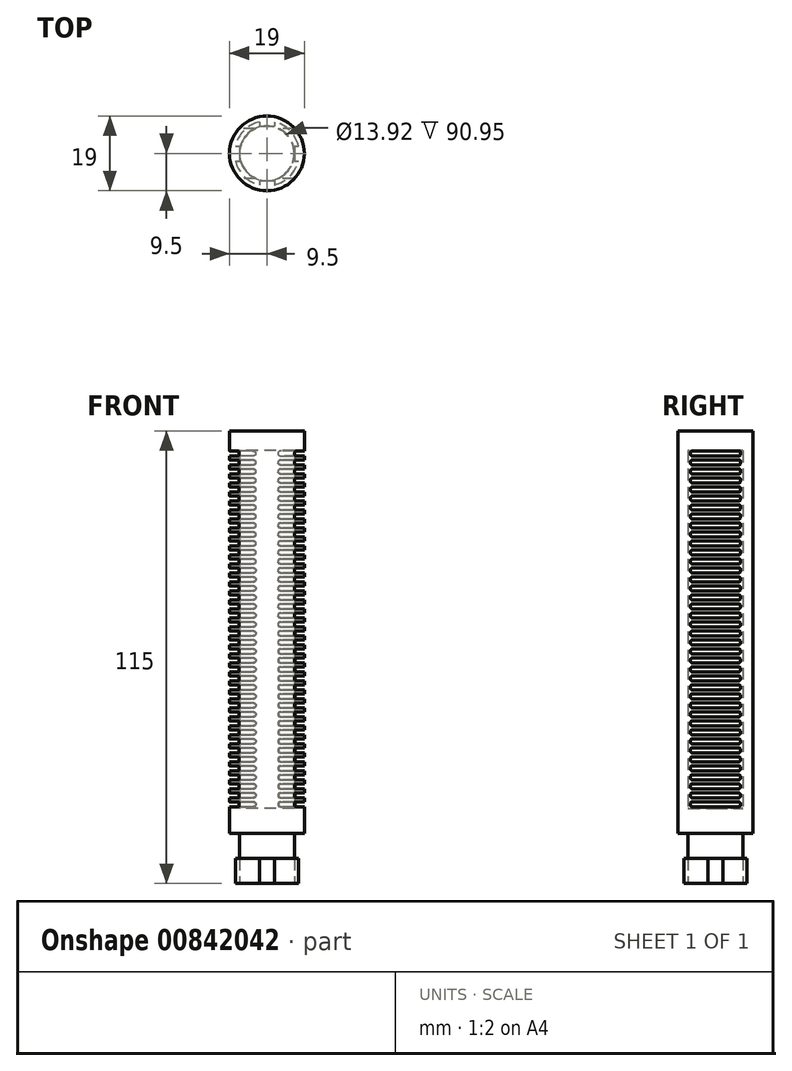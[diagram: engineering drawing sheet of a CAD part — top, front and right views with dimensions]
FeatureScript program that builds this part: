
annotation { "Feature Type Name" : "Feature", "Feature Type Description" : "" }
export const myFeature = defineFeature(function(context is Context, id is Id, definition is map)
    precondition{}
    {
        {
            var Q0;
            Q0=qCreatedBy(makeId("Top.planeOp"),FACE);
            var sketch = newSketch(context, id + "F0", { "sketchPlane" : qUnion([Q0])});
            skCircle(sketch, "E0", {"center": v(0, 0) * mm, "radius": 9.5 * mm});
            skSolve(sketch);
        }
        {
            var Q0;
            Q0 = qSketchRegion(id + "F0", true);
            extrude(context, id + "F1", {"entities" : qUnion([Q0]), "depth" : 115 * mm, "offsetDistance" : 25.4 * mm});
        }
        {
            var Q0;
            Q0=qCreatedBy(makeId("Top.planeOp"),FACE);
            var sketch = newSketch(context, id + "F2", { "sketchPlane" : qUnion([Q0])});
            skCircle(sketch, "E1", {"center": v(0, 0) * mm, "radius": 9.5 * mm});
            skCircle(sketch, "E2.0", {"center": v(0, 0) * mm, "radius": 6.96 * mm});
            skSolve(sketch);
        }
        {
            var Q0;
            Q0=makeQuery(id+"F2.imprint","IMPRINT",FACE,{"disambiguationData":[TD([[makeQuery(id+"F2.imprint","IMPRINT",EDGE,{"derivedFrom":sQuery(id+"F2.wireOp",EDGE,"E1")}),1.0]])]});
            extrude(context, id + "F3", {"entities" : qUnion([Q0]), "depth" : 12.7 * mm, "offsetDistance" : 25.4 * mm, "hasSecondDirection" : true, "secondDirectionOppositeDirection" : true, "secondDirectionDepth" : -6.35 * mm});
        }
        {
            var Q0;
            Q0=makeQuery(id+"F3.opExtrude","SWEPT_BODY",BODY,{"disambiguationData":[OSD([sQuery(id+"F2.wireOp",EDGE,"E1"),sQuery(id+"F2.wireOp",EDGE,"E2.0")])]});
            var Q1;
            Q1=makeQuery(id+"F1.opExtrude","SWEPT_BODY",BODY,{"disambiguationData":[OSD([sQuery(id+"F0.wireOp",EDGE,"E0")])]});
            booleanBodies(context, id + "F4", {"operationType" : BooleanOperationType.SUBTRACTION, "tools" : qUnion([Q0]), "targets" : qUnion([Q1])});
        }
        {
            var Q0;
            Q0=qCreatedBy(makeId("Top.planeOp"),FACE);
            var sketch = newSketch(context, id + "F5", { "sketchPlane" : qUnion([Q0])});
            skCircle(sketch, "E3", {"center": v(0, 0) * mm, "radius": 9.5 * mm});
            skCircle(sketch, "E4.0", {"center": v(0, 0) * mm, "radius": 8.23 * mm});
            skSolve(sketch);
        }
        {
            var Q0;
            Q0=makeQuery(id+"F5.imprint","IMPRINT",FACE,{"disambiguationData":[TD([[makeQuery(id+"F5.imprint","IMPRINT",EDGE,{"derivedFrom":sQuery(id+"F5.wireOp",EDGE,"E3")}),1.0]])]});
            extrude(context, id + "F6", {"entities" : qUnion([Q0]), "depth" : 6.35 * mm, "offsetDistance" : 25.4 * mm});
        }
        {
            var Q0;
            Q0=makeQuery(id+"F6.opExtrude","SWEPT_BODY",BODY,{"disambiguationData":[OSD([sQuery(id+"F5.wireOp",EDGE,"E3"),sQuery(id+"F5.wireOp",EDGE,"E4.0")])]});
            var Q1;
            Q1=makeQuery(id+"F1.opExtrude","SWEPT_BODY",BODY,{"disambiguationData":[OSD([sQuery(id+"F0.wireOp",EDGE,"E0")])]});
            booleanBodies(context, id + "F7", {"operationType" : BooleanOperationType.SUBTRACTION, "tools" : qUnion([Q0]), "targets" : qUnion([Q1])});
        }
        {
            var Q0;
            Q0=qCreatedBy(makeId("Top.planeOp"),FACE);
            var sketch = newSketch(context, id + "F8", { "sketchPlane" : qUnion([Q0])});
            skCircle(sketch, "E5", {"center": v(0, 0) * mm, "radius": 9.5 * mm, "construction": true});
            skCircle(sketch, "E6.0", {"center": v(0, 0) * mm, "radius": 6.96 * mm, "construction": true});
            skLineSegment(sketch, "E7.bottom", {"start": v(-1.9, 10.77) * mm, "end": v(1.9, 10.77) * mm});
            skLineSegment(sketch, "E7.top", {"start": v(-1.9, 6.96) * mm, "end": v(1.9, 6.96) * mm});
            skLineSegment(sketch, "E7.left", {"start": v(-1.9, 10.77) * mm, "end": v(-1.9, 6.96) * mm});
            skLineSegment(sketch, "E7.right", {"start": v(1.9, 10.77) * mm, "end": v(1.9, 6.96) * mm});
            skPoint(sketch, "E8", {"position": v(0, 6.96) * mm});
            skLineSegment(sketch, "E9.bottom", {"start": v(-9.5, 9.5) * mm, "end": v(9.5, 9.5) * mm, "construction": true});
            skLineSegment(sketch, "E9.top", {"start": v(-9.5, -9.5) * mm, "end": v(9.5, -9.5) * mm, "construction": true});
            skLineSegment(sketch, "E9.left", {"start": v(-9.5, 9.5) * mm, "end": v(-9.5, -9.5) * mm, "construction": true});
            skLineSegment(sketch, "E9.right", {"start": v(9.5, 9.5) * mm, "end": v(9.5, -9.5) * mm, "construction": true});
            skPoint(sketch, "E10", {"position": v(0, -9.5) * mm});
            skPoint(sketch, "E11", {"position": v(9.5, 0) * mm});
            skLineSegment(sketch, "E12.0", {"start": v(-6.96, 6.96) * mm, "end": v(-6.96, -6.96) * mm, "construction": true});
            skLineSegment(sketch, "E12.1", {"start": v(-6.96, 6.96) * mm, "end": v(6.96, 6.96) * mm, "construction": true});
            skLineSegment(sketch, "E12.2", {"start": v(6.96, 6.96) * mm, "end": v(6.96, -6.96) * mm, "construction": true});
            skLineSegment(sketch, "E12.3", {"start": v(-6.96, -6.96) * mm, "end": v(6.96, -6.96) * mm, "construction": true});
            skLineSegment(sketch, "E13.bottom", {"start": v(6.96, 1.9) * mm, "end": v(10.77, 1.9) * mm});
            skLineSegment(sketch, "E13.top", {"start": v(6.96, -1.9) * mm, "end": v(10.77, -1.9) * mm});
            skLineSegment(sketch, "E13.left", {"start": v(6.96, 1.9) * mm, "end": v(6.96, -1.9) * mm});
            skLineSegment(sketch, "E13.right", {"start": v(10.77, 1.9) * mm, "end": v(10.77, -1.9) * mm});
            skPoint(sketch, "E14", {"position": v(6.96, 0) * mm});
            skLineSegment(sketch, "E15.bottom", {"start": v(-1.9, -6.96) * mm, "end": v(1.9, -6.96) * mm});
            skLineSegment(sketch, "E15.top", {"start": v(-1.9, -10.77) * mm, "end": v(1.9, -10.77) * mm});
            skLineSegment(sketch, "E15.left", {"start": v(-1.9, -6.96) * mm, "end": v(-1.9, -10.77) * mm});
            skLineSegment(sketch, "E15.right", {"start": v(1.9, -6.96) * mm, "end": v(1.9, -10.77) * mm});
            skPoint(sketch, "E16", {"position": v(0, -6.96) * mm});
            skLineSegment(sketch, "E17.bottom", {"start": v(-10.77, 1.9) * mm, "end": v(-6.96, 1.9) * mm});
            skLineSegment(sketch, "E17.top", {"start": v(-10.77, -1.9) * mm, "end": v(-6.96, -1.9) * mm});
            skLineSegment(sketch, "E17.left", {"start": v(-10.77, 1.9) * mm, "end": v(-10.77, -1.9) * mm});
            skLineSegment(sketch, "E17.right", {"start": v(-6.96, 1.9) * mm, "end": v(-6.96, -1.9) * mm});
            skPoint(sketch, "E18", {"position": v(-6.96, 0) * mm});
            skSolve(sketch);
        }
        {
            var Q0;
            Q0=makeQuery(id+"F8.imprint","IMPRINT",FACE,{"disambiguationData":[TD([[makeQuery(id+"F8.imprint","IMPRINT",EDGE,{"derivedFrom":sQuery(id+"F8.wireOp",EDGE,"E17.bottom")}),-1.0]])]});
            var Q1;
            Q1=makeQuery(id+"F8.imprint","IMPRINT",FACE,{"disambiguationData":[TD([[makeQuery(id+"F8.imprint","IMPRINT",EDGE,{"derivedFrom":sQuery(id+"F8.wireOp",EDGE,"E7.bottom")}),-1.0]])]});
            var Q2;
            Q2=makeQuery(id+"F8.imprint","IMPRINT",FACE,{"disambiguationData":[TD([[makeQuery(id+"F8.imprint","IMPRINT",EDGE,{"derivedFrom":sQuery(id+"F8.wireOp",EDGE,"E13.bottom")}),-1.0]])]});
            var Q3;
            Q3=makeQuery(id+"F8.imprint","IMPRINT",FACE,{"disambiguationData":[TD([[makeQuery(id+"F8.imprint","IMPRINT",EDGE,{"derivedFrom":sQuery(id+"F8.wireOp",EDGE,"E15.bottom")}),-1.0]])]});
            extrude(context, id + "F9", {"entities" : qUnion([Q0, Q1, Q2, Q3]), "depth" : 6.35 * mm, "offsetDistance" : 25.4 * mm});
        }
        {
            var Q0;
            Q0=makeQuery(id+"F9.opExtrude","SWEPT_BODY",BODY,{"disambiguationData":[OSD([sQuery(id+"F8.wireOp",EDGE,"E7.bottom"),sQuery(id+"F8.wireOp",EDGE,"E7.top"),sQuery(id+"F8.wireOp",EDGE,"E7.left"),sQuery(id+"F8.wireOp",EDGE,"E7.right")])]});
            var Q1;
            Q1=makeQuery(id+"F9.opExtrude","SWEPT_BODY",BODY,{"disambiguationData":[OSD([sQuery(id+"F8.wireOp",EDGE,"E13.bottom"),sQuery(id+"F8.wireOp",EDGE,"E13.top"),sQuery(id+"F8.wireOp",EDGE,"E13.left"),sQuery(id+"F8.wireOp",EDGE,"E13.right")])]});
            var Q2;
            Q2=makeQuery(id+"F9.opExtrude","SWEPT_BODY",BODY,{"disambiguationData":[OSD([sQuery(id+"F8.wireOp",EDGE,"E15.bottom"),sQuery(id+"F8.wireOp",EDGE,"E15.top"),sQuery(id+"F8.wireOp",EDGE,"E15.left"),sQuery(id+"F8.wireOp",EDGE,"E15.right")])]});
            var Q3;
            Q3=makeQuery(id+"F9.opExtrude","SWEPT_BODY",BODY,{"disambiguationData":[OSD([sQuery(id+"F8.wireOp",EDGE,"E17.bottom"),sQuery(id+"F8.wireOp",EDGE,"E17.top"),sQuery(id+"F8.wireOp",EDGE,"E17.left"),sQuery(id+"F8.wireOp",EDGE,"E17.right")])]});
            var Q4;
            Q4=makeQuery(id+"F1.opExtrude","SWEPT_BODY",BODY,{"disambiguationData":[OSD([sQuery(id+"F0.wireOp",EDGE,"E0")])]});
            booleanBodies(context, id + "F10", {"operationType" : BooleanOperationType.SUBTRACTION, "tools" : qUnion([Q0, Q1, Q2, Q3]), "targets" : qUnion([Q4])});
        }
        {
            var Q0;
            Q0=qCreatedBy(makeId("Top.planeOp"),FACE);
            var sketch = newSketch(context, id + "F11", { "sketchPlane" : qUnion([Q0])});
            skCircle(sketch, "E19", {"center": v(0, 0) * mm, "radius": 9.5 * mm, "construction": true});
            skCircle(sketch, "E20.0", {"center": v(0, 0) * mm, "radius": 6.96 * mm});
            skSolve(sketch);
        }
        {
            var Q0;
            Q0=makeQuery(id+"F11.imprint","IMPRINT",FACE,{"disambiguationData":[TD([[makeQuery(id+"F11.imprint","IMPRINT",EDGE,{"derivedFrom":sQuery(id+"F11.wireOp",EDGE,"E20.0")}),1.0]])]});
            extrude(context, id + "F12", {"entities" : qUnion([Q0]), "operationType" : NewBodyOperationType.REMOVE, "depth" : 110 * mm, "offsetDistance" : 25.4 * mm, "hasSecondDirection" : true, "secondDirectionOppositeDirection" : true, "secondDirectionDepth" : -19.05 * mm});
        }
        {
            var Q0;
            Q0=qCreatedBy(makeId("Right.planeOp"),FACE);
            var sketch = newSketch(context, id + "F13", { "sketchPlane" : qUnion([Q0])});
            skLineSegment(sketch, "E21.bottom", {"start": v(5.91, 109.9) * mm, "end": v(-5.91, 109.9) * mm});
            skLineSegment(sketch, "E21.top", {"start": v(5.91, 108.63) * mm, "end": v(-5.91, 108.63) * mm});
            skLineSegment(sketch, "E21.left", {"start": v(6.35, 109.46) * mm, "end": v(6.35, 109.06) * mm});
            skLineSegment(sketch, "E21.right", {"start": v(-6.35, 109.46) * mm, "end": v(-6.35, 109.06) * mm});
            skPoint(sketch, "E22", {"position": v(0, 109.9) * mm});
            skPoint(sketch, "E23.visualSharp", {"position": v(6.35, 109.9) * mm});
            skArc(sketch, "E23.filletArc", {"start": v(6.35, 109.46) * mm, "mid": v(6.22, 109.77) * mm, "end": v(5.91, 109.9) * mm});
            skPoint(sketch, "E24.visualSharp", {"position": v(6.35, 108.63) * mm});
            skArc(sketch, "E24.filletArc", {"start": v(5.91, 108.63) * mm, "mid": v(6.22, 108.75) * mm, "end": v(6.35, 109.06) * mm});
            skPoint(sketch, "E25.visualSharp", {"position": v(-6.35, 108.63) * mm});
            skArc(sketch, "E25.filletArc", {"start": v(-6.35, 109.06) * mm, "mid": v(-6.22, 108.75) * mm, "end": v(-5.91, 108.63) * mm});
            skPoint(sketch, "E26.visualSharp", {"position": v(-6.35, 109.9) * mm});
            skArc(sketch, "E26.filletArc", {"start": v(-5.91, 109.9) * mm, "mid": v(-6.22, 109.77) * mm, "end": v(-6.35, 109.46) * mm});
            skArc(sketch, "E27.1.0.0", {"start": v(6.35, 107.17) * mm, "mid": v(6.22, 107.48) * mm, "end": v(5.9, 107.6) * mm});
            skLineSegment(sketch, "E27.1.0.1", {"start": v(5.9, 107.6) * mm, "end": v(-5.91, 107.6) * mm});
            skArc(sketch, "E27.1.0.2", {"start": v(-5.91, 107.6) * mm, "mid": v(-6.22, 107.48) * mm, "end": v(-6.35, 107.17) * mm});
            skLineSegment(sketch, "E27.1.0.3", {"start": v(-6.35, 107.17) * mm, "end": v(-6.35, 106.78) * mm});
            skArc(sketch, "E27.1.0.4", {"start": v(-6.35, 106.78) * mm, "mid": v(-6.22, 106.47) * mm, "end": v(-5.91, 106.34) * mm});
            skLineSegment(sketch, "E27.1.0.5", {"start": v(5.9, 106.34) * mm, "end": v(-5.91, 106.34) * mm});
            skArc(sketch, "E27.1.0.6", {"start": v(5.9, 106.34) * mm, "mid": v(6.22, 106.47) * mm, "end": v(6.35, 106.78) * mm});
            skLineSegment(sketch, "E27.1.0.7", {"start": v(6.35, 107.17) * mm, "end": v(6.35, 106.78) * mm});
            skArc(sketch, "E27.2.0.0", {"start": v(6.35, 104.88) * mm, "mid": v(6.22, 105.2) * mm, "end": v(5.9, 105.32) * mm});
            skLineSegment(sketch, "E27.2.0.1", {"start": v(5.9, 105.32) * mm, "end": v(-5.91, 105.32) * mm});
            skArc(sketch, "E27.2.0.2", {"start": v(-5.91, 105.32) * mm, "mid": v(-6.22, 105.2) * mm, "end": v(-6.35, 104.88) * mm});
            skLineSegment(sketch, "E27.2.0.3", {"start": v(-6.35, 104.88) * mm, "end": v(-6.35, 104.5) * mm});
            skArc(sketch, "E27.2.0.4", {"start": v(-6.35, 104.5) * mm, "mid": v(-6.22, 104.18) * mm, "end": v(-5.91, 104.05) * mm});
            skLineSegment(sketch, "E27.2.0.5", {"start": v(5.9, 104.05) * mm, "end": v(-5.91, 104.05) * mm});
            skArc(sketch, "E27.2.0.6", {"start": v(5.9, 104.05) * mm, "mid": v(6.22, 104.18) * mm, "end": v(6.35, 104.5) * mm});
            skLineSegment(sketch, "E27.2.0.7", {"start": v(6.35, 104.88) * mm, "end": v(6.35, 104.5) * mm});
            skArc(sketch, "E27.3.0.0", {"start": v(6.35, 102.6) * mm, "mid": v(6.22, 102.9) * mm, "end": v(5.9, 103.04) * mm});
            skLineSegment(sketch, "E27.3.0.1", {"start": v(5.9, 103.04) * mm, "end": v(-5.91, 103.04) * mm});
            skArc(sketch, "E27.3.0.2", {"start": v(-5.91, 103.04) * mm, "mid": v(-6.22, 102.9) * mm, "end": v(-6.35, 102.6) * mm});
            skLineSegment(sketch, "E27.3.0.3", {"start": v(-6.35, 102.6) * mm, "end": v(-6.35, 102.2) * mm});
            skArc(sketch, "E27.3.0.4", {"start": v(-6.35, 102.2) * mm, "mid": v(-6.22, 101.9) * mm, "end": v(-5.91, 101.77) * mm});
            skLineSegment(sketch, "E27.3.0.5", {"start": v(5.9, 101.77) * mm, "end": v(-5.91, 101.77) * mm});
            skArc(sketch, "E27.3.0.6", {"start": v(5.9, 101.77) * mm, "mid": v(6.22, 101.9) * mm, "end": v(6.35, 102.2) * mm});
            skLineSegment(sketch, "E27.3.0.7", {"start": v(6.35, 102.6) * mm, "end": v(6.35, 102.2) * mm});
            skArc(sketch, "E27.4.0.0", {"start": v(6.35, 100.31) * mm, "mid": v(6.22, 100.62) * mm, "end": v(5.9, 100.75) * mm});
            skLineSegment(sketch, "E27.4.0.1", {"start": v(5.9, 100.75) * mm, "end": v(-5.91, 100.75) * mm});
            skArc(sketch, "E27.4.0.2", {"start": v(-5.91, 100.75) * mm, "mid": v(-6.22, 100.62) * mm, "end": v(-6.35, 100.31) * mm});
            skLineSegment(sketch, "E27.4.0.3", {"start": v(-6.35, 100.31) * mm, "end": v(-6.35, 99.92) * mm});
            skArc(sketch, "E27.4.0.4", {"start": v(-6.35, 99.92) * mm, "mid": v(-6.22, 99.61) * mm, "end": v(-5.91, 99.48) * mm});
            skLineSegment(sketch, "E27.4.0.5", {"start": v(5.9, 99.48) * mm, "end": v(-5.91, 99.48) * mm});
            skArc(sketch, "E27.4.0.6", {"start": v(5.9, 99.48) * mm, "mid": v(6.22, 99.61) * mm, "end": v(6.35, 99.92) * mm});
            skLineSegment(sketch, "E27.4.0.7", {"start": v(6.35, 100.31) * mm, "end": v(6.35, 99.92) * mm});
            skArc(sketch, "E27.5.0.0", {"start": v(6.35, 98.03) * mm, "mid": v(6.22, 98.34) * mm, "end": v(5.9, 98.47) * mm});
            skLineSegment(sketch, "E27.5.0.1", {"start": v(5.9, 98.47) * mm, "end": v(-5.91, 98.47) * mm});
            skArc(sketch, "E27.5.0.2", {"start": v(-5.91, 98.47) * mm, "mid": v(-6.23, 98.34) * mm, "end": v(-6.35, 98.03) * mm});
            skLineSegment(sketch, "E27.5.0.3", {"start": v(-6.35, 98.03) * mm, "end": v(-6.35, 97.63) * mm});
            skArc(sketch, "E27.5.0.4", {"start": v(-6.35, 97.63) * mm, "mid": v(-6.23, 97.32) * mm, "end": v(-5.91, 97.2) * mm});
            skLineSegment(sketch, "E27.5.0.5", {"start": v(5.9, 97.2) * mm, "end": v(-5.91, 97.2) * mm});
            skArc(sketch, "E27.5.0.6", {"start": v(5.9, 97.2) * mm, "mid": v(6.22, 97.32) * mm, "end": v(6.35, 97.63) * mm});
            skLineSegment(sketch, "E27.5.0.7", {"start": v(6.35, 98.03) * mm, "end": v(6.35, 97.63) * mm});
            skArc(sketch, "E27.6.0.0", {"start": v(6.34, 95.74) * mm, "mid": v(6.22, 96.05) * mm, "end": v(5.9, 96.18) * mm});
            skLineSegment(sketch, "E27.6.0.1", {"start": v(5.9, 96.18) * mm, "end": v(-5.92, 96.18) * mm});
            skArc(sketch, "E27.6.0.2", {"start": v(-5.92, 96.18) * mm, "mid": v(-6.23, 96.05) * mm, "end": v(-6.36, 95.74) * mm});
            skLineSegment(sketch, "E27.6.0.3", {"start": v(-6.36, 95.74) * mm, "end": v(-6.36, 95.35) * mm});
            skArc(sketch, "E27.6.0.4", {"start": v(-6.36, 95.35) * mm, "mid": v(-6.23, 95.04) * mm, "end": v(-5.92, 94.9) * mm});
            skLineSegment(sketch, "E27.6.0.5", {"start": v(5.9, 94.9) * mm, "end": v(-5.92, 94.9) * mm});
            skArc(sketch, "E27.6.0.6", {"start": v(5.9, 94.9) * mm, "mid": v(6.22, 95.04) * mm, "end": v(6.34, 95.35) * mm});
            skLineSegment(sketch, "E27.6.0.7", {"start": v(6.34, 95.74) * mm, "end": v(6.34, 95.35) * mm});
            skArc(sketch, "E27.7.0.0", {"start": v(6.34, 93.45) * mm, "mid": v(6.22, 93.77) * mm, "end": v(5.9, 93.9) * mm});
            skLineSegment(sketch, "E27.7.0.1", {"start": v(5.9, 93.9) * mm, "end": v(-5.92, 93.9) * mm});
            skArc(sketch, "E27.7.0.2", {"start": v(-5.92, 93.9) * mm, "mid": v(-6.23, 93.77) * mm, "end": v(-6.36, 93.45) * mm});
            skLineSegment(sketch, "E27.7.0.3", {"start": v(-6.36, 93.45) * mm, "end": v(-6.36, 93.06) * mm});
            skArc(sketch, "E27.7.0.4", {"start": v(-6.36, 93.06) * mm, "mid": v(-6.23, 92.75) * mm, "end": v(-5.92, 92.62) * mm});
            skLineSegment(sketch, "E27.7.0.5", {"start": v(5.9, 92.62) * mm, "end": v(-5.92, 92.62) * mm});
            skArc(sketch, "E27.7.0.6", {"start": v(5.9, 92.62) * mm, "mid": v(6.22, 92.75) * mm, "end": v(6.34, 93.06) * mm});
            skLineSegment(sketch, "E27.7.0.7", {"start": v(6.34, 93.45) * mm, "end": v(6.34, 93.06) * mm});
            skArc(sketch, "E27.8.0.0", {"start": v(6.34, 91.17) * mm, "mid": v(6.21, 91.48) * mm, "end": v(5.9, 91.6) * mm});
            skLineSegment(sketch, "E27.8.0.1", {"start": v(5.9, 91.6) * mm, "end": v(-5.92, 91.6) * mm});
            skArc(sketch, "E27.8.0.2", {"start": v(-5.92, 91.6) * mm, "mid": v(-6.23, 91.48) * mm, "end": v(-6.36, 91.17) * mm});
            skLineSegment(sketch, "E27.8.0.3", {"start": v(-6.36, 91.17) * mm, "end": v(-6.36, 90.78) * mm});
            skArc(sketch, "E27.8.0.4", {"start": v(-6.36, 90.78) * mm, "mid": v(-6.23, 90.47) * mm, "end": v(-5.92, 90.34) * mm});
            skLineSegment(sketch, "E27.8.0.5", {"start": v(5.9, 90.34) * mm, "end": v(-5.92, 90.34) * mm});
            skArc(sketch, "E27.8.0.6", {"start": v(5.9, 90.34) * mm, "mid": v(6.21, 90.47) * mm, "end": v(6.34, 90.78) * mm});
            skLineSegment(sketch, "E27.8.0.7", {"start": v(6.34, 91.17) * mm, "end": v(6.34, 90.78) * mm});
            skArc(sketch, "E27.9.0.0", {"start": v(6.34, 88.88) * mm, "mid": v(6.21, 89.2) * mm, "end": v(5.9, 89.32) * mm});
            skLineSegment(sketch, "E27.9.0.1", {"start": v(5.9, 89.32) * mm, "end": v(-5.92, 89.32) * mm});
            skArc(sketch, "E27.9.0.2", {"start": v(-5.92, 89.32) * mm, "mid": v(-6.23, 89.2) * mm, "end": v(-6.36, 88.88) * mm});
            skLineSegment(sketch, "E27.9.0.3", {"start": v(-6.36, 88.88) * mm, "end": v(-6.36, 88.5) * mm});
            skArc(sketch, "E27.9.0.4", {"start": v(-6.36, 88.5) * mm, "mid": v(-6.23, 88.18) * mm, "end": v(-5.92, 88.05) * mm});
            skLineSegment(sketch, "E27.9.0.5", {"start": v(5.9, 88.05) * mm, "end": v(-5.92, 88.05) * mm});
            skArc(sketch, "E27.9.0.6", {"start": v(5.9, 88.05) * mm, "mid": v(6.21, 88.18) * mm, "end": v(6.34, 88.5) * mm});
            skLineSegment(sketch, "E27.9.0.7", {"start": v(6.34, 88.88) * mm, "end": v(6.34, 88.5) * mm});
            skArc(sketch, "E27.10.0.0", {"start": v(6.34, 86.6) * mm, "mid": v(6.21, 86.9) * mm, "end": v(5.9, 87.04) * mm});
            skLineSegment(sketch, "E27.10.0.1", {"start": v(5.9, 87.04) * mm, "end": v(-5.92, 87.04) * mm});
            skArc(sketch, "E27.10.0.2", {"start": v(-5.92, 87.04) * mm, "mid": v(-6.23, 86.9) * mm, "end": v(-6.36, 86.6) * mm});
            skLineSegment(sketch, "E27.10.0.3", {"start": v(-6.36, 86.6) * mm, "end": v(-6.36, 86.2) * mm});
            skArc(sketch, "E27.10.0.4", {"start": v(-6.36, 86.2) * mm, "mid": v(-6.23, 85.9) * mm, "end": v(-5.92, 85.77) * mm});
            skLineSegment(sketch, "E27.10.0.5", {"start": v(5.9, 85.77) * mm, "end": v(-5.92, 85.77) * mm});
            skArc(sketch, "E27.10.0.6", {"start": v(5.9, 85.77) * mm, "mid": v(6.21, 85.9) * mm, "end": v(6.34, 86.2) * mm});
            skLineSegment(sketch, "E27.10.0.7", {"start": v(6.34, 86.6) * mm, "end": v(6.34, 86.2) * mm});
            skArc(sketch, "E27.11.0.0", {"start": v(6.34, 84.31) * mm, "mid": v(6.21, 84.62) * mm, "end": v(5.9, 84.75) * mm});
            skLineSegment(sketch, "E27.11.0.1", {"start": v(5.9, 84.75) * mm, "end": v(-5.92, 84.75) * mm});
            skArc(sketch, "E27.11.0.2", {"start": v(-5.92, 84.75) * mm, "mid": v(-6.23, 84.62) * mm, "end": v(-6.36, 84.31) * mm});
            skLineSegment(sketch, "E27.11.0.3", {"start": v(-6.36, 84.31) * mm, "end": v(-6.36, 83.92) * mm});
            skArc(sketch, "E27.11.0.4", {"start": v(-6.36, 83.92) * mm, "mid": v(-6.23, 83.6) * mm, "end": v(-5.92, 83.48) * mm});
            skLineSegment(sketch, "E27.11.0.5", {"start": v(5.9, 83.48) * mm, "end": v(-5.92, 83.48) * mm});
            skArc(sketch, "E27.11.0.6", {"start": v(5.9, 83.48) * mm, "mid": v(6.21, 83.6) * mm, "end": v(6.34, 83.92) * mm});
            skLineSegment(sketch, "E27.11.0.7", {"start": v(6.34, 84.31) * mm, "end": v(6.34, 83.92) * mm});
            skArc(sketch, "E27.12.0.0", {"start": v(6.34, 82.02) * mm, "mid": v(6.21, 82.34) * mm, "end": v(5.9, 82.46) * mm});
            skLineSegment(sketch, "E27.12.0.1", {"start": v(5.9, 82.46) * mm, "end": v(-5.92, 82.46) * mm});
            skArc(sketch, "E27.12.0.2", {"start": v(-5.92, 82.46) * mm, "mid": v(-6.23, 82.34) * mm, "end": v(-6.36, 82.02) * mm});
            skLineSegment(sketch, "E27.12.0.3", {"start": v(-6.36, 82.02) * mm, "end": v(-6.36, 81.63) * mm});
            skArc(sketch, "E27.12.0.4", {"start": v(-6.36, 81.63) * mm, "mid": v(-6.23, 81.32) * mm, "end": v(-5.92, 81.2) * mm});
            skLineSegment(sketch, "E27.12.0.5", {"start": v(5.9, 81.2) * mm, "end": v(-5.92, 81.2) * mm});
            skArc(sketch, "E27.12.0.6", {"start": v(5.9, 81.2) * mm, "mid": v(6.21, 81.32) * mm, "end": v(6.34, 81.63) * mm});
            skLineSegment(sketch, "E27.12.0.7", {"start": v(6.34, 82.02) * mm, "end": v(6.34, 81.63) * mm});
            skArc(sketch, "E27.13.0.0", {"start": v(6.34, 79.74) * mm, "mid": v(6.21, 80.05) * mm, "end": v(5.9, 80.18) * mm});
            skLineSegment(sketch, "E27.13.0.1", {"start": v(5.9, 80.18) * mm, "end": v(-5.92, 80.18) * mm});
            skArc(sketch, "E27.13.0.2", {"start": v(-5.92, 80.18) * mm, "mid": v(-6.23, 80.05) * mm, "end": v(-6.36, 79.74) * mm});
            skLineSegment(sketch, "E27.13.0.3", {"start": v(-6.36, 79.74) * mm, "end": v(-6.36, 79.35) * mm});
            skArc(sketch, "E27.13.0.4", {"start": v(-6.36, 79.35) * mm, "mid": v(-6.23, 79.04) * mm, "end": v(-5.92, 78.9) * mm});
            skLineSegment(sketch, "E27.13.0.5", {"start": v(5.9, 78.9) * mm, "end": v(-5.92, 78.9) * mm});
            skArc(sketch, "E27.13.0.6", {"start": v(5.9, 78.9) * mm, "mid": v(6.21, 79.04) * mm, "end": v(6.34, 79.35) * mm});
            skLineSegment(sketch, "E27.13.0.7", {"start": v(6.34, 79.74) * mm, "end": v(6.34, 79.35) * mm});
            skArc(sketch, "E27.14.0.0", {"start": v(6.34, 77.45) * mm, "mid": v(6.2, 77.76) * mm, "end": v(5.9, 77.9) * mm});
            skLineSegment(sketch, "E27.14.0.1", {"start": v(5.9, 77.9) * mm, "end": v(-5.92, 77.9) * mm});
            skArc(sketch, "E27.14.0.2", {"start": v(-5.92, 77.9) * mm, "mid": v(-6.23, 77.76) * mm, "end": v(-6.36, 77.45) * mm});
            skLineSegment(sketch, "E27.14.0.3", {"start": v(-6.36, 77.45) * mm, "end": v(-6.36, 77.06) * mm});
            skArc(sketch, "E27.14.0.4", {"start": v(-6.36, 77.06) * mm, "mid": v(-6.23, 76.75) * mm, "end": v(-5.92, 76.62) * mm});
            skLineSegment(sketch, "E27.14.0.5", {"start": v(5.9, 76.62) * mm, "end": v(-5.92, 76.62) * mm});
            skArc(sketch, "E27.14.0.6", {"start": v(5.9, 76.62) * mm, "mid": v(6.2, 76.75) * mm, "end": v(6.34, 77.06) * mm});
            skLineSegment(sketch, "E27.14.0.7", {"start": v(6.34, 77.45) * mm, "end": v(6.34, 77.06) * mm});
            skArc(sketch, "E27.15.0.0", {"start": v(6.34, 75.17) * mm, "mid": v(6.2, 75.48) * mm, "end": v(5.9, 75.6) * mm});
            skLineSegment(sketch, "E27.15.0.1", {"start": v(5.9, 75.6) * mm, "end": v(-5.92, 75.6) * mm});
            skArc(sketch, "E27.15.0.2", {"start": v(-5.92, 75.6) * mm, "mid": v(-6.23, 75.48) * mm, "end": v(-6.36, 75.17) * mm});
            skLineSegment(sketch, "E27.15.0.3", {"start": v(-6.36, 75.17) * mm, "end": v(-6.36, 74.77) * mm});
            skArc(sketch, "E27.15.0.4", {"start": v(-6.36, 74.77) * mm, "mid": v(-6.23, 74.46) * mm, "end": v(-5.92, 74.34) * mm});
            skLineSegment(sketch, "E27.15.0.5", {"start": v(5.9, 74.34) * mm, "end": v(-5.92, 74.34) * mm});
            skArc(sketch, "E27.15.0.6", {"start": v(5.9, 74.34) * mm, "mid": v(6.2, 74.46) * mm, "end": v(6.34, 74.77) * mm});
            skLineSegment(sketch, "E27.15.0.7", {"start": v(6.34, 75.17) * mm, "end": v(6.34, 74.77) * mm});
            skArc(sketch, "E27.16.0.0", {"start": v(6.34, 72.88) * mm, "mid": v(6.2, 73.2) * mm, "end": v(5.9, 73.32) * mm});
            skLineSegment(sketch, "E27.16.0.1", {"start": v(5.9, 73.32) * mm, "end": v(-5.92, 73.32) * mm});
            skArc(sketch, "E27.16.0.2", {"start": v(-5.92, 73.32) * mm, "mid": v(-6.23, 73.2) * mm, "end": v(-6.36, 72.88) * mm});
            skLineSegment(sketch, "E27.16.0.3", {"start": v(-6.36, 72.88) * mm, "end": v(-6.36, 72.49) * mm});
            skArc(sketch, "E27.16.0.4", {"start": v(-6.36, 72.49) * mm, "mid": v(-6.23, 72.18) * mm, "end": v(-5.92, 72.05) * mm});
            skLineSegment(sketch, "E27.16.0.5", {"start": v(5.9, 72.05) * mm, "end": v(-5.92, 72.05) * mm});
            skArc(sketch, "E27.16.0.6", {"start": v(5.9, 72.05) * mm, "mid": v(6.2, 72.18) * mm, "end": v(6.34, 72.49) * mm});
            skLineSegment(sketch, "E27.16.0.7", {"start": v(6.34, 72.88) * mm, "end": v(6.34, 72.49) * mm});
            skArc(sketch, "E27.17.0.0", {"start": v(6.34, 70.6) * mm, "mid": v(6.2, 70.9) * mm, "end": v(5.9, 71.03) * mm});
            skLineSegment(sketch, "E27.17.0.1", {"start": v(5.9, 71.03) * mm, "end": v(-5.93, 71.03) * mm});
            skArc(sketch, "E27.17.0.2", {"start": v(-5.93, 71.03) * mm, "mid": v(-6.24, 70.9) * mm, "end": v(-6.36, 70.6) * mm});
            skLineSegment(sketch, "E27.17.0.3", {"start": v(-6.36, 70.6) * mm, "end": v(-6.36, 70.2) * mm});
            skArc(sketch, "E27.17.0.4", {"start": v(-6.36, 70.2) * mm, "mid": v(-6.24, 69.9) * mm, "end": v(-5.93, 69.76) * mm});
            skLineSegment(sketch, "E27.17.0.5", {"start": v(5.9, 69.76) * mm, "end": v(-5.93, 69.76) * mm});
            skArc(sketch, "E27.17.0.6", {"start": v(5.9, 69.76) * mm, "mid": v(6.2, 69.9) * mm, "end": v(6.34, 70.2) * mm});
            skLineSegment(sketch, "E27.17.0.7", {"start": v(6.34, 70.6) * mm, "end": v(6.34, 70.2) * mm});
            skArc(sketch, "E27.18.0.0", {"start": v(6.33, 68.3) * mm, "mid": v(6.2, 68.62) * mm, "end": v(5.9, 68.75) * mm});
            skLineSegment(sketch, "E27.18.0.1", {"start": v(5.9, 68.75) * mm, "end": v(-5.93, 68.75) * mm});
            skArc(sketch, "E27.18.0.2", {"start": v(-5.93, 68.75) * mm, "mid": v(-6.24, 68.62) * mm, "end": v(-6.37, 68.3) * mm});
            skLineSegment(sketch, "E27.18.0.3", {"start": v(-6.37, 68.3) * mm, "end": v(-6.37, 67.92) * mm});
            skArc(sketch, "E27.18.0.4", {"start": v(-6.37, 67.92) * mm, "mid": v(-6.24, 67.6) * mm, "end": v(-5.93, 67.48) * mm});
            skLineSegment(sketch, "E27.18.0.5", {"start": v(5.9, 67.48) * mm, "end": v(-5.93, 67.48) * mm});
            skArc(sketch, "E27.18.0.6", {"start": v(5.9, 67.48) * mm, "mid": v(6.2, 67.6) * mm, "end": v(6.33, 67.92) * mm});
            skLineSegment(sketch, "E27.18.0.7", {"start": v(6.33, 68.3) * mm, "end": v(6.33, 67.92) * mm});
            skArc(sketch, "E27.19.0.0", {"start": v(6.33, 66.02) * mm, "mid": v(6.2, 66.33) * mm, "end": v(5.9, 66.46) * mm});
            skLineSegment(sketch, "E27.19.0.1", {"start": v(5.9, 66.46) * mm, "end": v(-5.93, 66.46) * mm});
            skArc(sketch, "E27.19.0.2", {"start": v(-5.93, 66.46) * mm, "mid": v(-6.24, 66.33) * mm, "end": v(-6.37, 66.02) * mm});
            skLineSegment(sketch, "E27.19.0.3", {"start": v(-6.37, 66.02) * mm, "end": v(-6.37, 65.63) * mm});
            skArc(sketch, "E27.19.0.4", {"start": v(-6.37, 65.63) * mm, "mid": v(-6.24, 65.32) * mm, "end": v(-5.93, 65.2) * mm});
            skLineSegment(sketch, "E27.19.0.5", {"start": v(5.9, 65.2) * mm, "end": v(-5.93, 65.2) * mm});
            skArc(sketch, "E27.19.0.6", {"start": v(5.9, 65.2) * mm, "mid": v(6.2, 65.32) * mm, "end": v(6.33, 65.63) * mm});
            skLineSegment(sketch, "E27.19.0.7", {"start": v(6.33, 66.02) * mm, "end": v(6.33, 65.63) * mm});
            skArc(sketch, "E27.20.0.0", {"start": v(6.33, 63.74) * mm, "mid": v(6.2, 64.05) * mm, "end": v(5.9, 64.18) * mm});
            skLineSegment(sketch, "E27.20.0.1", {"start": v(5.9, 64.18) * mm, "end": v(-5.93, 64.18) * mm});
            skArc(sketch, "E27.20.0.2", {"start": v(-5.93, 64.18) * mm, "mid": v(-6.24, 64.05) * mm, "end": v(-6.37, 63.74) * mm});
            skLineSegment(sketch, "E27.20.0.3", {"start": v(-6.37, 63.74) * mm, "end": v(-6.37, 63.34) * mm});
            skArc(sketch, "E27.20.0.4", {"start": v(-6.37, 63.34) * mm, "mid": v(-6.24, 63.03) * mm, "end": v(-5.93, 62.9) * mm});
            skLineSegment(sketch, "E27.20.0.5", {"start": v(5.9, 62.9) * mm, "end": v(-5.93, 62.9) * mm});
            skArc(sketch, "E27.20.0.6", {"start": v(5.9, 62.9) * mm, "mid": v(6.2, 63.03) * mm, "end": v(6.33, 63.34) * mm});
            skLineSegment(sketch, "E27.20.0.7", {"start": v(6.33, 63.74) * mm, "end": v(6.33, 63.34) * mm});
            skArc(sketch, "E27.21.0.0", {"start": v(6.33, 61.45) * mm, "mid": v(6.2, 61.76) * mm, "end": v(5.9, 61.89) * mm});
            skLineSegment(sketch, "E27.21.0.1", {"start": v(5.9, 61.89) * mm, "end": v(-5.93, 61.89) * mm});
            skArc(sketch, "E27.21.0.2", {"start": v(-5.93, 61.89) * mm, "mid": v(-6.24, 61.76) * mm, "end": v(-6.37, 61.45) * mm});
            skLineSegment(sketch, "E27.21.0.3", {"start": v(-6.37, 61.45) * mm, "end": v(-6.37, 61.06) * mm});
            skArc(sketch, "E27.21.0.4", {"start": v(-6.37, 61.06) * mm, "mid": v(-6.24, 60.75) * mm, "end": v(-5.93, 60.62) * mm});
            skLineSegment(sketch, "E27.21.0.5", {"start": v(5.9, 60.62) * mm, "end": v(-5.93, 60.62) * mm});
            skArc(sketch, "E27.21.0.6", {"start": v(5.9, 60.62) * mm, "mid": v(6.2, 60.75) * mm, "end": v(6.33, 61.06) * mm});
            skLineSegment(sketch, "E27.21.0.7", {"start": v(6.33, 61.45) * mm, "end": v(6.33, 61.06) * mm});
            skArc(sketch, "E27.22.0.0", {"start": v(6.33, 59.16) * mm, "mid": v(6.2, 59.48) * mm, "end": v(5.9, 59.6) * mm});
            skLineSegment(sketch, "E27.22.0.1", {"start": v(5.9, 59.6) * mm, "end": v(-5.93, 59.6) * mm});
            skArc(sketch, "E27.22.0.2", {"start": v(-5.93, 59.6) * mm, "mid": v(-6.24, 59.48) * mm, "end": v(-6.37, 59.16) * mm});
            skLineSegment(sketch, "E27.22.0.3", {"start": v(-6.37, 59.16) * mm, "end": v(-6.37, 58.77) * mm});
            skArc(sketch, "E27.22.0.4", {"start": v(-6.37, 58.77) * mm, "mid": v(-6.24, 58.46) * mm, "end": v(-5.93, 58.33) * mm});
            skLineSegment(sketch, "E27.22.0.5", {"start": v(5.9, 58.33) * mm, "end": v(-5.93, 58.33) * mm});
            skArc(sketch, "E27.22.0.6", {"start": v(5.9, 58.33) * mm, "mid": v(6.2, 58.46) * mm, "end": v(6.33, 58.77) * mm});
            skLineSegment(sketch, "E27.22.0.7", {"start": v(6.33, 59.16) * mm, "end": v(6.33, 58.77) * mm});
            skArc(sketch, "E27.23.0.0", {"start": v(6.33, 56.88) * mm, "mid": v(6.2, 57.19) * mm, "end": v(5.9, 57.32) * mm});
            skLineSegment(sketch, "E27.23.0.1", {"start": v(5.9, 57.32) * mm, "end": v(-5.93, 57.32) * mm});
            skArc(sketch, "E27.23.0.2", {"start": v(-5.93, 57.32) * mm, "mid": v(-6.24, 57.19) * mm, "end": v(-6.37, 56.88) * mm});
            skLineSegment(sketch, "E27.23.0.3", {"start": v(-6.37, 56.88) * mm, "end": v(-6.37, 56.49) * mm});
            skArc(sketch, "E27.23.0.4", {"start": v(-6.37, 56.49) * mm, "mid": v(-6.24, 56.18) * mm, "end": v(-5.93, 56.05) * mm});
            skLineSegment(sketch, "E27.23.0.5", {"start": v(5.9, 56.05) * mm, "end": v(-5.93, 56.05) * mm});
            skArc(sketch, "E27.23.0.6", {"start": v(5.9, 56.05) * mm, "mid": v(6.2, 56.18) * mm, "end": v(6.33, 56.49) * mm});
            skLineSegment(sketch, "E27.23.0.7", {"start": v(6.33, 56.88) * mm, "end": v(6.33, 56.49) * mm});
            skArc(sketch, "E27.24.0.0", {"start": v(6.33, 54.6) * mm, "mid": v(6.2, 54.9) * mm, "end": v(5.9, 55.03) * mm});
            skLineSegment(sketch, "E27.24.0.1", {"start": v(5.9, 55.03) * mm, "end": v(-5.93, 55.03) * mm});
            skArc(sketch, "E27.24.0.2", {"start": v(-5.93, 55.03) * mm, "mid": v(-6.24, 54.9) * mm, "end": v(-6.37, 54.6) * mm});
            skLineSegment(sketch, "E27.24.0.3", {"start": v(-6.37, 54.6) * mm, "end": v(-6.37, 54.2) * mm});
            skArc(sketch, "E27.24.0.4", {"start": v(-6.37, 54.2) * mm, "mid": v(-6.24, 53.9) * mm, "end": v(-5.93, 53.76) * mm});
            skLineSegment(sketch, "E27.24.0.5", {"start": v(5.9, 53.76) * mm, "end": v(-5.93, 53.76) * mm});
            skArc(sketch, "E27.24.0.6", {"start": v(5.9, 53.76) * mm, "mid": v(6.2, 53.9) * mm, "end": v(6.33, 54.2) * mm});
            skLineSegment(sketch, "E27.24.0.7", {"start": v(6.33, 54.6) * mm, "end": v(6.33, 54.2) * mm});
            skArc(sketch, "E27.25.0.0", {"start": v(6.33, 52.3) * mm, "mid": v(6.2, 52.62) * mm, "end": v(5.89, 52.75) * mm});
            skLineSegment(sketch, "E27.25.0.1", {"start": v(5.89, 52.75) * mm, "end": v(-5.93, 52.75) * mm});
            skArc(sketch, "E27.25.0.2", {"start": v(-5.93, 52.75) * mm, "mid": v(-6.24, 52.62) * mm, "end": v(-6.37, 52.3) * mm});
            skLineSegment(sketch, "E27.25.0.3", {"start": v(-6.37, 52.3) * mm, "end": v(-6.37, 51.91) * mm});
            skArc(sketch, "E27.25.0.4", {"start": v(-6.37, 51.91) * mm, "mid": v(-6.24, 51.6) * mm, "end": v(-5.93, 51.48) * mm});
            skLineSegment(sketch, "E27.25.0.5", {"start": v(5.89, 51.48) * mm, "end": v(-5.93, 51.48) * mm});
            skArc(sketch, "E27.25.0.6", {"start": v(5.89, 51.48) * mm, "mid": v(6.2, 51.6) * mm, "end": v(6.33, 51.91) * mm});
            skLineSegment(sketch, "E27.25.0.7", {"start": v(6.33, 52.3) * mm, "end": v(6.33, 51.91) * mm});
            skArc(sketch, "E27.26.0.0", {"start": v(6.33, 50.02) * mm, "mid": v(6.2, 50.33) * mm, "end": v(5.89, 50.46) * mm});
            skLineSegment(sketch, "E27.26.0.1", {"start": v(5.89, 50.46) * mm, "end": v(-5.93, 50.46) * mm});
            skArc(sketch, "E27.26.0.2", {"start": v(-5.93, 50.46) * mm, "mid": v(-6.24, 50.33) * mm, "end": v(-6.37, 50.02) * mm});
            skLineSegment(sketch, "E27.26.0.3", {"start": v(-6.37, 50.02) * mm, "end": v(-6.37, 49.63) * mm});
            skArc(sketch, "E27.26.0.4", {"start": v(-6.37, 49.63) * mm, "mid": v(-6.24, 49.32) * mm, "end": v(-5.93, 49.19) * mm});
            skLineSegment(sketch, "E27.26.0.5", {"start": v(5.89, 49.19) * mm, "end": v(-5.93, 49.19) * mm});
            skArc(sketch, "E27.26.0.6", {"start": v(5.89, 49.19) * mm, "mid": v(6.2, 49.32) * mm, "end": v(6.33, 49.63) * mm});
            skLineSegment(sketch, "E27.26.0.7", {"start": v(6.33, 50.02) * mm, "end": v(6.33, 49.63) * mm});
            skArc(sketch, "E27.27.0.0", {"start": v(6.33, 47.73) * mm, "mid": v(6.2, 48.05) * mm, "end": v(5.89, 48.17) * mm});
            skLineSegment(sketch, "E27.27.0.1", {"start": v(5.89, 48.17) * mm, "end": v(-5.93, 48.17) * mm});
            skArc(sketch, "E27.27.0.2", {"start": v(-5.93, 48.17) * mm, "mid": v(-6.24, 48.05) * mm, "end": v(-6.37, 47.73) * mm});
            skLineSegment(sketch, "E27.27.0.3", {"start": v(-6.37, 47.73) * mm, "end": v(-6.37, 47.34) * mm});
            skArc(sketch, "E27.27.0.4", {"start": v(-6.37, 47.34) * mm, "mid": v(-6.24, 47.03) * mm, "end": v(-5.93, 46.9) * mm});
            skLineSegment(sketch, "E27.27.0.5", {"start": v(5.89, 46.9) * mm, "end": v(-5.93, 46.9) * mm});
            skArc(sketch, "E27.27.0.6", {"start": v(5.89, 46.9) * mm, "mid": v(6.2, 47.03) * mm, "end": v(6.33, 47.34) * mm});
            skLineSegment(sketch, "E27.27.0.7", {"start": v(6.33, 47.73) * mm, "end": v(6.33, 47.34) * mm});
            skArc(sketch, "E27.28.0.0", {"start": v(6.33, 45.45) * mm, "mid": v(6.2, 45.76) * mm, "end": v(5.89, 45.89) * mm});
            skLineSegment(sketch, "E27.28.0.1", {"start": v(5.89, 45.89) * mm, "end": v(-5.93, 45.89) * mm});
            skArc(sketch, "E27.28.0.2", {"start": v(-5.93, 45.89) * mm, "mid": v(-6.24, 45.76) * mm, "end": v(-6.37, 45.45) * mm});
            skLineSegment(sketch, "E27.28.0.3", {"start": v(-6.37, 45.45) * mm, "end": v(-6.37, 45.06) * mm});
            skArc(sketch, "E27.28.0.4", {"start": v(-6.37, 45.06) * mm, "mid": v(-6.24, 44.75) * mm, "end": v(-5.93, 44.62) * mm});
            skLineSegment(sketch, "E27.28.0.5", {"start": v(5.89, 44.62) * mm, "end": v(-5.93, 44.62) * mm});
            skArc(sketch, "E27.28.0.6", {"start": v(5.89, 44.62) * mm, "mid": v(6.2, 44.75) * mm, "end": v(6.33, 45.06) * mm});
            skLineSegment(sketch, "E27.28.0.7", {"start": v(6.33, 45.45) * mm, "end": v(6.33, 45.06) * mm});
            skArc(sketch, "E27.29.0.0", {"start": v(6.33, 43.16) * mm, "mid": v(6.2, 43.47) * mm, "end": v(5.89, 43.6) * mm});
            skLineSegment(sketch, "E27.29.0.1", {"start": v(5.89, 43.6) * mm, "end": v(-5.94, 43.6) * mm});
            skArc(sketch, "E27.29.0.2", {"start": v(-5.94, 43.6) * mm, "mid": v(-6.25, 43.47) * mm, "end": v(-6.37, 43.16) * mm});
            skLineSegment(sketch, "E27.29.0.3", {"start": v(-6.37, 43.16) * mm, "end": v(-6.37, 42.77) * mm});
            skArc(sketch, "E27.29.0.4", {"start": v(-6.37, 42.77) * mm, "mid": v(-6.25, 42.46) * mm, "end": v(-5.94, 42.33) * mm});
            skLineSegment(sketch, "E27.29.0.5", {"start": v(5.89, 42.33) * mm, "end": v(-5.94, 42.33) * mm});
            skArc(sketch, "E27.29.0.6", {"start": v(5.89, 42.33) * mm, "mid": v(6.2, 42.46) * mm, "end": v(6.33, 42.77) * mm});
            skLineSegment(sketch, "E27.29.0.7", {"start": v(6.33, 43.16) * mm, "end": v(6.33, 42.77) * mm});
            skArc(sketch, "E27.30.0.0", {"start": v(6.32, 40.88) * mm, "mid": v(6.2, 41.19) * mm, "end": v(5.89, 41.32) * mm});
            skLineSegment(sketch, "E27.30.0.1", {"start": v(5.89, 41.32) * mm, "end": v(-5.94, 41.32) * mm});
            skArc(sketch, "E27.30.0.2", {"start": v(-5.94, 41.32) * mm, "mid": v(-6.25, 41.19) * mm, "end": v(-6.38, 40.88) * mm});
            skLineSegment(sketch, "E27.30.0.3", {"start": v(-6.38, 40.88) * mm, "end": v(-6.38, 40.48) * mm});
            skArc(sketch, "E27.30.0.4", {"start": v(-6.38, 40.48) * mm, "mid": v(-6.25, 40.17) * mm, "end": v(-5.94, 40.05) * mm});
            skLineSegment(sketch, "E27.30.0.5", {"start": v(5.89, 40.05) * mm, "end": v(-5.94, 40.05) * mm});
            skArc(sketch, "E27.30.0.6", {"start": v(5.89, 40.05) * mm, "mid": v(6.2, 40.17) * mm, "end": v(6.32, 40.48) * mm});
            skLineSegment(sketch, "E27.30.0.7", {"start": v(6.32, 40.88) * mm, "end": v(6.32, 40.48) * mm});
            skArc(sketch, "E27.31.0.0", {"start": v(6.32, 38.6) * mm, "mid": v(6.2, 38.9) * mm, "end": v(5.88, 39.03) * mm});
            skLineSegment(sketch, "E27.31.0.1", {"start": v(5.88, 39.03) * mm, "end": v(-5.94, 39.03) * mm});
            skArc(sketch, "E27.31.0.2", {"start": v(-5.94, 39.03) * mm, "mid": v(-6.25, 38.9) * mm, "end": v(-6.38, 38.6) * mm});
            skLineSegment(sketch, "E27.31.0.3", {"start": v(-6.38, 38.6) * mm, "end": v(-6.38, 38.2) * mm});
            skArc(sketch, "E27.31.0.4", {"start": v(-6.38, 38.2) * mm, "mid": v(-6.25, 37.89) * mm, "end": v(-5.94, 37.76) * mm});
            skLineSegment(sketch, "E27.31.0.5", {"start": v(5.88, 37.76) * mm, "end": v(-5.94, 37.76) * mm});
            skArc(sketch, "E27.31.0.6", {"start": v(5.88, 37.76) * mm, "mid": v(6.2, 37.89) * mm, "end": v(6.32, 38.2) * mm});
            skLineSegment(sketch, "E27.31.0.7", {"start": v(6.32, 38.6) * mm, "end": v(6.32, 38.2) * mm});
            skArc(sketch, "E27.32.0.0", {"start": v(6.32, 36.3) * mm, "mid": v(6.2, 36.62) * mm, "end": v(5.88, 36.74) * mm});
            skLineSegment(sketch, "E27.32.0.1", {"start": v(5.88, 36.74) * mm, "end": v(-5.94, 36.74) * mm});
            skArc(sketch, "E27.32.0.2", {"start": v(-5.94, 36.74) * mm, "mid": v(-6.25, 36.62) * mm, "end": v(-6.38, 36.3) * mm});
            skLineSegment(sketch, "E27.32.0.3", {"start": v(-6.38, 36.3) * mm, "end": v(-6.38, 35.91) * mm});
            skArc(sketch, "E27.32.0.4", {"start": v(-6.38, 35.91) * mm, "mid": v(-6.25, 35.6) * mm, "end": v(-5.94, 35.47) * mm});
            skLineSegment(sketch, "E27.32.0.5", {"start": v(5.88, 35.47) * mm, "end": v(-5.94, 35.47) * mm});
            skArc(sketch, "E27.32.0.6", {"start": v(5.88, 35.47) * mm, "mid": v(6.2, 35.6) * mm, "end": v(6.32, 35.91) * mm});
            skLineSegment(sketch, "E27.32.0.7", {"start": v(6.32, 36.3) * mm, "end": v(6.32, 35.91) * mm});
            skArc(sketch, "E27.33.0.0", {"start": v(6.32, 34.02) * mm, "mid": v(6.2, 34.33) * mm, "end": v(5.88, 34.46) * mm});
            skLineSegment(sketch, "E27.33.0.1", {"start": v(5.88, 34.46) * mm, "end": v(-5.94, 34.46) * mm});
            skArc(sketch, "E27.33.0.2", {"start": v(-5.94, 34.46) * mm, "mid": v(-6.25, 34.33) * mm, "end": v(-6.38, 34.02) * mm});
            skLineSegment(sketch, "E27.33.0.3", {"start": v(-6.38, 34.02) * mm, "end": v(-6.38, 33.63) * mm});
            skArc(sketch, "E27.33.0.4", {"start": v(-6.38, 33.63) * mm, "mid": v(-6.25, 33.32) * mm, "end": v(-5.94, 33.19) * mm});
            skLineSegment(sketch, "E27.33.0.5", {"start": v(5.88, 33.19) * mm, "end": v(-5.94, 33.19) * mm});
            skArc(sketch, "E27.33.0.6", {"start": v(5.88, 33.19) * mm, "mid": v(6.2, 33.32) * mm, "end": v(6.32, 33.63) * mm});
            skLineSegment(sketch, "E27.33.0.7", {"start": v(6.32, 34.02) * mm, "end": v(6.32, 33.63) * mm});
            skArc(sketch, "E27.34.0.0", {"start": v(6.32, 31.73) * mm, "mid": v(6.2, 32.04) * mm, "end": v(5.88, 32.17) * mm});
            skLineSegment(sketch, "E27.34.0.1", {"start": v(5.88, 32.17) * mm, "end": v(-5.94, 32.17) * mm});
            skArc(sketch, "E27.34.0.2", {"start": v(-5.94, 32.17) * mm, "mid": v(-6.25, 32.04) * mm, "end": v(-6.38, 31.73) * mm});
            skLineSegment(sketch, "E27.34.0.3", {"start": v(-6.38, 31.73) * mm, "end": v(-6.38, 31.34) * mm});
            skArc(sketch, "E27.34.0.4", {"start": v(-6.38, 31.34) * mm, "mid": v(-6.25, 31.03) * mm, "end": v(-5.94, 30.9) * mm});
            skLineSegment(sketch, "E27.34.0.5", {"start": v(5.88, 30.9) * mm, "end": v(-5.94, 30.9) * mm});
            skArc(sketch, "E27.34.0.6", {"start": v(5.88, 30.9) * mm, "mid": v(6.2, 31.03) * mm, "end": v(6.32, 31.34) * mm});
            skLineSegment(sketch, "E27.34.0.7", {"start": v(6.32, 31.73) * mm, "end": v(6.32, 31.34) * mm});
            skArc(sketch, "E27.35.0.0", {"start": v(6.32, 29.45) * mm, "mid": v(6.2, 29.76) * mm, "end": v(5.88, 29.89) * mm});
            skLineSegment(sketch, "E27.35.0.1", {"start": v(5.88, 29.89) * mm, "end": v(-5.94, 29.89) * mm});
            skArc(sketch, "E27.35.0.2", {"start": v(-5.94, 29.89) * mm, "mid": v(-6.25, 29.76) * mm, "end": v(-6.38, 29.45) * mm});
            skLineSegment(sketch, "E27.35.0.3", {"start": v(-6.38, 29.45) * mm, "end": v(-6.38, 29.05) * mm});
            skArc(sketch, "E27.35.0.4", {"start": v(-6.38, 29.05) * mm, "mid": v(-6.25, 28.74) * mm, "end": v(-5.94, 28.62) * mm});
            skLineSegment(sketch, "E27.35.0.5", {"start": v(5.88, 28.62) * mm, "end": v(-5.94, 28.62) * mm});
            skArc(sketch, "E27.35.0.6", {"start": v(5.88, 28.62) * mm, "mid": v(6.2, 28.74) * mm, "end": v(6.32, 29.05) * mm});
            skLineSegment(sketch, "E27.35.0.7", {"start": v(6.32, 29.45) * mm, "end": v(6.32, 29.05) * mm});
            skArc(sketch, "E27.36.0.0", {"start": v(6.32, 27.16) * mm, "mid": v(6.2, 27.47) * mm, "end": v(5.88, 27.6) * mm});
            skLineSegment(sketch, "E27.36.0.1", {"start": v(5.88, 27.6) * mm, "end": v(-5.94, 27.6) * mm});
            skArc(sketch, "E27.36.0.2", {"start": v(-5.94, 27.6) * mm, "mid": v(-6.25, 27.47) * mm, "end": v(-6.38, 27.16) * mm});
            skLineSegment(sketch, "E27.36.0.3", {"start": v(-6.38, 27.16) * mm, "end": v(-6.38, 26.77) * mm});
            skArc(sketch, "E27.36.0.4", {"start": v(-6.38, 26.77) * mm, "mid": v(-6.25, 26.46) * mm, "end": v(-5.94, 26.33) * mm});
            skLineSegment(sketch, "E27.36.0.5", {"start": v(5.88, 26.33) * mm, "end": v(-5.94, 26.33) * mm});
            skArc(sketch, "E27.36.0.6", {"start": v(5.88, 26.33) * mm, "mid": v(6.2, 26.46) * mm, "end": v(6.32, 26.77) * mm});
            skLineSegment(sketch, "E27.36.0.7", {"start": v(6.32, 27.16) * mm, "end": v(6.32, 26.77) * mm});
            skArc(sketch, "E27.37.0.0", {"start": v(6.32, 24.87) * mm, "mid": v(6.2, 25.19) * mm, "end": v(5.88, 25.31) * mm});
            skLineSegment(sketch, "E27.37.0.1", {"start": v(5.88, 25.31) * mm, "end": v(-5.94, 25.31) * mm});
            skArc(sketch, "E27.37.0.2", {"start": v(-5.94, 25.31) * mm, "mid": v(-6.25, 25.19) * mm, "end": v(-6.38, 24.87) * mm});
            skLineSegment(sketch, "E27.37.0.3", {"start": v(-6.38, 24.87) * mm, "end": v(-6.38, 24.48) * mm});
            skArc(sketch, "E27.37.0.4", {"start": v(-6.38, 24.48) * mm, "mid": v(-6.25, 24.17) * mm, "end": v(-5.94, 24.04) * mm});
            skLineSegment(sketch, "E27.37.0.5", {"start": v(5.88, 24.04) * mm, "end": v(-5.94, 24.04) * mm});
            skArc(sketch, "E27.37.0.6", {"start": v(5.88, 24.04) * mm, "mid": v(6.2, 24.17) * mm, "end": v(6.32, 24.48) * mm});
            skLineSegment(sketch, "E27.37.0.7", {"start": v(6.32, 24.87) * mm, "end": v(6.32, 24.48) * mm});
            skArc(sketch, "E27.38.0.0", {"start": v(6.32, 22.59) * mm, "mid": v(6.19, 22.9) * mm, "end": v(5.88, 23.03) * mm});
            skLineSegment(sketch, "E27.38.0.1", {"start": v(5.88, 23.03) * mm, "end": v(-5.94, 23.03) * mm});
            skArc(sketch, "E27.38.0.2", {"start": v(-5.94, 23.03) * mm, "mid": v(-6.25, 22.9) * mm, "end": v(-6.38, 22.59) * mm});
            skLineSegment(sketch, "E27.38.0.3", {"start": v(-6.38, 22.59) * mm, "end": v(-6.38, 22.2) * mm});
            skArc(sketch, "E27.38.0.4", {"start": v(-6.38, 22.2) * mm, "mid": v(-6.25, 21.89) * mm, "end": v(-5.94, 21.76) * mm});
            skLineSegment(sketch, "E27.38.0.5", {"start": v(5.88, 21.76) * mm, "end": v(-5.94, 21.76) * mm});
            skArc(sketch, "E27.38.0.6", {"start": v(5.88, 21.76) * mm, "mid": v(6.19, 21.89) * mm, "end": v(6.32, 22.2) * mm});
            skLineSegment(sketch, "E27.38.0.7", {"start": v(6.32, 22.59) * mm, "end": v(6.32, 22.2) * mm});
            skArc(sketch, "E27.39.0.0", {"start": v(6.32, 20.3) * mm, "mid": v(6.19, 20.61) * mm, "end": v(5.88, 20.74) * mm});
            skLineSegment(sketch, "E27.39.0.1", {"start": v(5.88, 20.74) * mm, "end": v(-5.94, 20.74) * mm});
            skArc(sketch, "E27.39.0.2", {"start": v(-5.94, 20.74) * mm, "mid": v(-6.25, 20.61) * mm, "end": v(-6.38, 20.3) * mm});
            skLineSegment(sketch, "E27.39.0.3", {"start": v(-6.38, 20.3) * mm, "end": v(-6.38, 19.91) * mm});
            skArc(sketch, "E27.39.0.4", {"start": v(-6.38, 19.91) * mm, "mid": v(-6.25, 19.6) * mm, "end": v(-5.94, 19.47) * mm});
            skLineSegment(sketch, "E27.39.0.5", {"start": v(5.88, 19.47) * mm, "end": v(-5.94, 19.47) * mm});
            skArc(sketch, "E27.39.0.6", {"start": v(5.88, 19.47) * mm, "mid": v(6.19, 19.6) * mm, "end": v(6.32, 19.91) * mm});
            skLineSegment(sketch, "E27.39.0.7", {"start": v(6.32, 20.3) * mm, "end": v(6.32, 19.91) * mm});
            skLineSegment(sketch, "E27.direction1", {"start": v(-5.91, 108.63) * mm, "end": v(-5.91, 106.34) * mm, "construction": true});
            skSolve(sketch);
        }
        {
            var Q0;
            Q0 = qSketchRegion(id + "F13", true);
            extrude(context, id + "F14", {"entities" : qUnion([Q0]), "operationType" : NewBodyOperationType.REMOVE, "depth" : 12.7 * mm, "offsetDistance" : 25.4 * mm, "hasSecondDirection" : true, "secondDirectionOppositeDirection" : true, "secondDirectionDepth" : 12.7 * mm});
        }
    });
